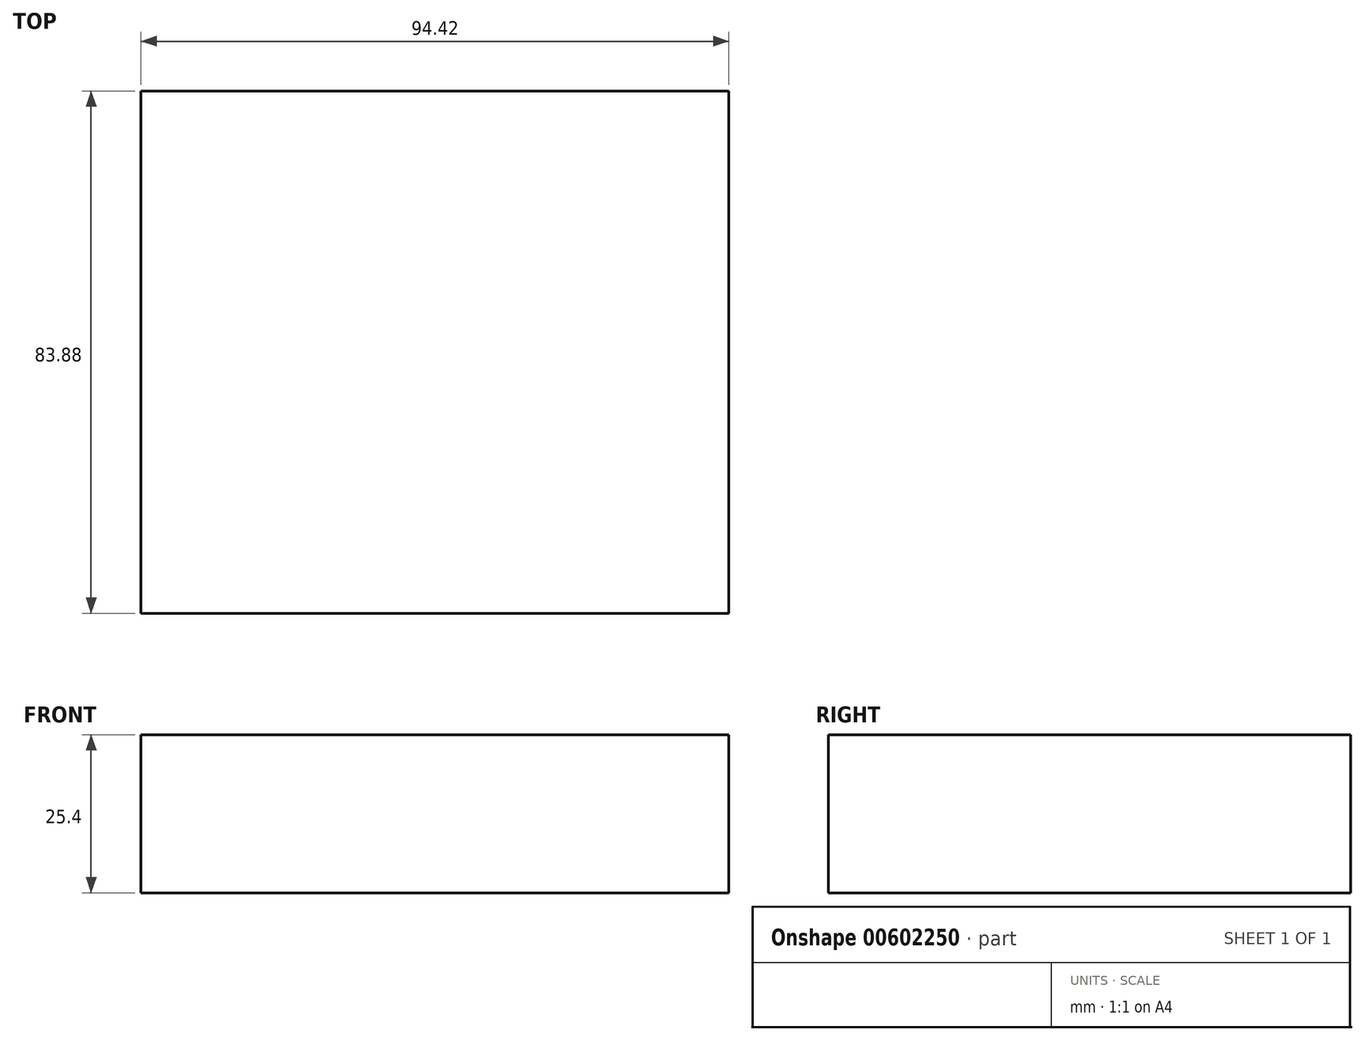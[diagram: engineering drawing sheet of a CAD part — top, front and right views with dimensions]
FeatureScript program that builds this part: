
annotation { "Feature Type Name" : "Feature", "Feature Type Description" : "" }
export const myFeature = defineFeature(function(context is Context, id is Id, definition is map)
    precondition{}
    {
        {
            var Q0;
            Q0=qCreatedBy(makeId("Top.planeOp"),FACE);
            var sketch = newSketch(context, id + "F0", { "sketchPlane" : qUnion([Q0])});
            skLineSegment(sketch, "E0.bottom", {"start": v(47.21, 41.94) * mm, "end": v(-47.21, 41.94) * mm});
            skLineSegment(sketch, "E0.top", {"start": v(47.21, -41.94) * mm, "end": v(-47.21, -41.94) * mm});
            skLineSegment(sketch, "E0.left", {"start": v(47.21, 41.94) * mm, "end": v(47.21, -41.94) * mm});
            skLineSegment(sketch, "E0.right", {"start": v(-47.21, 41.94) * mm, "end": v(-47.21, -41.94) * mm});
            skPoint(sketch, "E0.middle", {"position": v(0, 0) * mm});
            skSolve(sketch);
        }
        {
            var Q0;
            Q0 = qSketchRegion(id + "F0", true);
            extrude(context, id + "F1", {"entities" : qUnion([Q0]), "endBound" : BoundingType.SYMMETRIC, "depth" : 25.4 * mm, "offsetDistance" : 25.4 * mm});
        }
    });
